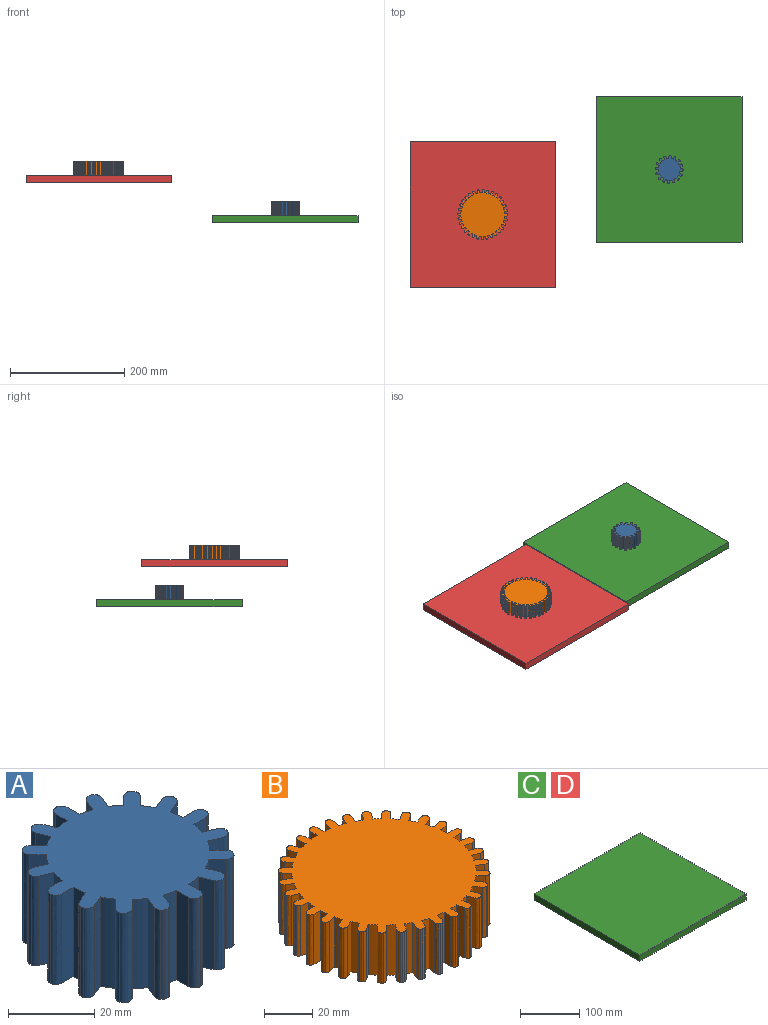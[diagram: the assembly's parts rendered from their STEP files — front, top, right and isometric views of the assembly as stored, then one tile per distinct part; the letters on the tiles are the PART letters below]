
ASSEMBLY  parts=4 mates=2
PART A: 114 faces, bbox 49.3x49.3x25.4 mm
  f0: plane 25.4x3.81mm, normal (-1,0,0), area 96.8mm2, adj f5,f6,f7,f8
  f1: plane 25.4x4.01mm, normal (1,0,0), area 101.9mm2, adj f2,f6,f7,f9
  f2: extruded ~25.4x1.56mm, area 48.5mm2, adj f1,f3,f6,f7
  f3: extruded ~25.4x0.92mm, area 24.5mm2, adj f2,f4,f6,f7
  f4: extruded ~25.4x0.92mm, area 24.5mm2, adj f3,f5,f6,f7
  f5: extruded ~25.4x1.57mm, area 48.5mm2, adj f0,f4,f6,f7
  f6: plane 49.31x49.31mm, normal (0,0,1), area 1458.4mm2, adj f0,f1,f2,f3,f4,f5,f8,f9
  f7: plane 49.31x49.31mm, normal (0,0,-1), area 1458.4mm2, adj f0,f1,f2,f3,f4,f5,f8,f9
  f8: cylinder r=19.05mm len=25.4mm, axis (0,0,-1), area 93mm2, adj f0,f6,f7,f109
  f9: cylinder r=19.05mm len=25.4mm, axis (0,0,-1), area 93mm2, adj f1,f6,f7,f24
  f10: cylinder r=19.05mm len=25.4mm, axis (0,0,-1), area 93mm2, adj f6,f7,f103,f108
  f11: cylinder r=19.05mm len=25.4mm, axis (0,0,-1), area 93mm2, adj f6,f7,f97,f102
  f12: cylinder r=19.05mm len=25.4mm, axis (0,0,-1), area 93mm2, adj f6,f7,f91,f96
  f13: cylinder r=19.05mm len=25.4mm, axis (0,0,-1), area 93mm2, adj f6,f7,f85,f90
  f14: cylinder r=19.05mm len=25.4mm, axis (0,0,-1), area 93mm2, adj f6,f7,f79,f84
  f15: cylinder r=19.05mm len=25.4mm, axis (0,0,-1), area 93mm2, adj f6,f7,f73,f78
  f16: cylinder r=19.05mm len=25.4mm, axis (0,0,-1), area 93mm2, adj f6,f7,f67,f72
  f17: cylinder r=19.05mm len=25.4mm, axis (0,0,-1), area 93mm2, adj f6,f7,f61,f66
  f18: cylinder r=19.05mm len=25.4mm, axis (0,0,-1), area 93mm2, adj f6,f7,f55,f60
  f19: cylinder r=19.05mm len=25.4mm, axis (0,0,-1), area 93mm2, adj f6,f7,f49,f54
  f20: cylinder r=19.05mm len=25.4mm, axis (0,0,-1), area 93mm2, adj f6,f7,f43,f48
  f21: cylinder r=19.05mm len=25.4mm, axis (0,0,-1), area 93mm2, adj f6,f7,f37,f42
  f22: cylinder r=19.05mm len=25.4mm, axis (0,0,-1), area 93mm2, adj f6,f7,f31,f36
  f23: cylinder r=19.05mm len=25.4mm, axis (0,0,-1), area 93mm2, adj f6,f7,f25,f30
  f24: plane 25.4x3.52mm, normal (-0.92,0.38,0), area 96.8mm2, adj f6,f7,f9,f29
  f25: plane 25.4x3.71mm, normal (0.92,-0.38,0), area 101.9mm2, adj f6,f7,f23,f26
  f26: extruded ~25.4x1.82mm, area 48.5mm2, adj f6,f7,f25,f27
  f27: extruded ~25.4x0.76mm, area 24.5mm2, adj f6,f7,f26,f28
  f28: extruded ~25.4x0.94mm, area 24.5mm2, adj f6,f7,f27,f29
  f29: extruded ~25.4x1.51mm, area 48.5mm2, adj f6,f7,f24,f28
  f30: plane 25.4x2.69mm, normal (-0.71,0.71,0), area 96.8mm2, adj f6,f7,f23,f35
  f31: plane 25.4x2.84mm, normal (0.71,-0.71,0), area 101.9mm2, adj f6,f7,f22,f32
  f32: extruded ~25.4x1.8mm, area 48.5mm2, adj f6,f7,f31,f33
  f33: extruded ~25.4x0.82mm, area 24.5mm2, adj f6,f7,f32,f34
  f34: extruded ~25.4x0.82mm, area 24.5mm2, adj f6,f7,f33,f35
  f35: extruded ~25.4x1.8mm, area 48.5mm2, adj f6,f7,f30,f34
  f36: plane 25.4x3.52mm, normal (-0.38,0.92,0), area 96.8mm2, adj f6,f7,f22,f41
  f37: plane 25.4x3.71mm, normal (0.38,-0.92,0), area 101.9mm2, adj f6,f7,f21,f38
  f38: extruded ~25.4x1.51mm, area 48.5mm2, adj f6,f7,f37,f39
  f39: extruded ~25.4x0.94mm, area 24.5mm2, adj f6,f7,f38,f40
  f40: extruded ~25.4x0.76mm, area 24.5mm2, adj f6,f7,f39,f41
  f41: extruded ~25.4x1.82mm, area 48.5mm2, adj f6,f7,f36,f40
  f42: plane 25.4x3.81mm, normal (0,1,0), area 96.8mm2, adj f6,f7,f21,f47
  f43: plane 25.4x4.01mm, normal (0,-1,0), area 101.9mm2, adj f6,f7,f20,f44
  f44: extruded ~25.4x1.56mm, area 48.5mm2, adj f6,f7,f43,f45
  f45: extruded ~25.4x0.92mm, area 24.5mm2, adj f6,f7,f44,f46
  f46: extruded ~25.4x0.92mm, area 24.5mm2, adj f6,f7,f45,f47
  f47: extruded ~25.4x1.57mm, area 48.5mm2, adj f6,f7,f42,f46
  f48: plane 25.4x3.52mm, normal (0.38,0.92,0), area 96.8mm2, adj f6,f7,f20,f53
  f49: plane 25.4x3.71mm, normal (-0.38,-0.92,0), area 101.9mm2, adj f6,f7,f19,f50
  f50: extruded ~25.4x1.82mm, area 48.5mm2, adj f6,f7,f49,f51
  f51: extruded ~25.4x0.76mm, area 24.5mm2, adj f6,f7,f50,f52
  f52: extruded ~25.4x0.94mm, area 24.5mm2, adj f6,f7,f51,f53
  f53: extruded ~25.4x1.51mm, area 48.5mm2, adj f6,f7,f48,f52
  f54: plane 25.4x2.69mm, normal (0.71,0.71,0), area 96.8mm2, adj f6,f7,f19,f59
  f55: plane 25.4x2.84mm, normal (-0.71,-0.71,0), area 101.9mm2, adj f6,f7,f18,f56
  f56: extruded ~25.4x1.8mm, area 48.5mm2, adj f6,f7,f55,f57
  f57: extruded ~25.4x0.82mm, area 24.5mm2, adj f6,f7,f56,f58
  f58: extruded ~25.4x0.82mm, area 24.5mm2, adj f6,f7,f57,f59
  f59: extruded ~25.4x1.8mm, area 48.5mm2, adj f6,f7,f54,f58
  f60: plane 25.4x3.52mm, normal (0.92,0.38,0), area 96.8mm2, adj f6,f7,f18,f65
  f61: plane 25.4x3.71mm, normal (-0.92,-0.38,0), area 101.9mm2, adj f6,f7,f17,f62
  f62: extruded ~25.4x1.51mm, area 48.5mm2, adj f6,f7,f61,f63
  f63: extruded ~25.4x0.94mm, area 24.5mm2, adj f6,f7,f62,f64
  f64: extruded ~25.4x0.76mm, area 24.5mm2, adj f6,f7,f63,f65
  f65: extruded ~25.4x1.82mm, area 48.5mm2, adj f6,f7,f60,f64
  f66: plane 25.4x3.81mm, normal (1,0,0), area 96.8mm2, adj f6,f7,f17,f71
  f67: plane 25.4x4.01mm, normal (-1,0,0), area 101.9mm2, adj f6,f7,f16,f68
  f68: extruded ~25.4x1.56mm, area 48.5mm2, adj f6,f7,f67,f69
  f69: extruded ~25.4x0.92mm, area 24.5mm2, adj f6,f7,f68,f70
  f70: extruded ~25.4x0.92mm, area 24.5mm2, adj f6,f7,f69,f71
  f71: extruded ~25.4x1.57mm, area 48.5mm2, adj f6,f7,f66,f70
  f72: plane 25.4x3.52mm, normal (0.92,-0.38,0), area 96.8mm2, adj f6,f7,f16,f77
  f73: plane 25.4x3.71mm, normal (-0.92,0.38,0), area 101.9mm2, adj f6,f7,f15,f74
  f74: extruded ~25.4x1.82mm, area 48.5mm2, adj f6,f7,f73,f75
  f75: extruded ~25.4x0.76mm, area 24.5mm2, adj f6,f7,f74,f76
  f76: extruded ~25.4x0.94mm, area 24.5mm2, adj f6,f7,f75,f77
  f77: extruded ~25.4x1.51mm, area 48.5mm2, adj f6,f7,f72,f76
  f78: plane 25.4x2.69mm, normal (0.71,-0.71,0), area 96.8mm2, adj f6,f7,f15,f83
  f79: plane 25.4x2.84mm, normal (-0.71,0.71,0), area 101.9mm2, adj f6,f7,f14,f80
  f80: extruded ~25.4x1.8mm, area 48.5mm2, adj f6,f7,f79,f81
  f81: extruded ~25.4x0.82mm, area 24.5mm2, adj f6,f7,f80,f82
  f82: extruded ~25.4x0.82mm, area 24.5mm2, adj f6,f7,f81,f83
  f83: extruded ~25.4x1.8mm, area 48.5mm2, adj f6,f7,f78,f82
  f84: plane 25.4x3.52mm, normal (0.38,-0.92,0), area 96.8mm2, adj f6,f7,f14,f89
  f85: plane 25.4x3.71mm, normal (-0.38,0.92,0), area 101.9mm2, adj f6,f7,f13,f86
  f86: extruded ~25.4x1.51mm, area 48.5mm2, adj f6,f7,f85,f87
  f87: extruded ~25.4x0.94mm, area 24.5mm2, adj f6,f7,f86,f88
  f88: extruded ~25.4x0.76mm, area 24.5mm2, adj f6,f7,f87,f89
  f89: extruded ~25.4x1.82mm, area 48.5mm2, adj f6,f7,f84,f88
  f90: plane 25.4x3.81mm, normal (0,-1,0), area 96.8mm2, adj f6,f7,f13,f95
  f91: plane 25.4x4.01mm, normal (0,1,0), area 101.9mm2, adj f6,f7,f12,f92
  f92: extruded ~25.4x1.56mm, area 48.5mm2, adj f6,f7,f91,f93
  f93: extruded ~25.4x0.92mm, area 24.5mm2, adj f6,f7,f92,f94
  f94: extruded ~25.4x0.92mm, area 24.5mm2, adj f6,f7,f93,f95
  f95: extruded ~25.4x1.57mm, area 48.5mm2, adj f6,f7,f90,f94
  f96: plane 25.4x3.52mm, normal (-0.38,-0.92,0), area 96.8mm2, adj f6,f7,f12,f101
  f97: plane 25.4x3.71mm, normal (0.38,0.92,0), area 101.9mm2, adj f6,f7,f11,f98
  f98: extruded ~25.4x1.82mm, area 48.5mm2, adj f6,f7,f97,f99
  f99: extruded ~25.4x0.76mm, area 24.5mm2, adj f6,f7,f98,f100
  f100: extruded ~25.4x0.94mm, area 24.5mm2, adj f6,f7,f99,f101
  f101: extruded ~25.4x1.51mm, area 48.5mm2, adj f6,f7,f96,f100
  f102: plane 25.4x2.69mm, normal (-0.71,-0.71,0), area 96.8mm2, adj f6,f7,f11,f107
  f103: plane 25.4x2.84mm, normal (0.71,0.71,0), area 101.9mm2, adj f6,f7,f10,f104
  f104: extruded ~25.4x1.8mm, area 48.5mm2, adj f6,f7,f103,f105
  f105: extruded ~25.4x0.82mm, area 24.5mm2, adj f6,f7,f104,f106
  f106: extruded ~25.4x0.82mm, area 24.5mm2, adj f6,f7,f105,f107
  f107: extruded ~25.4x1.8mm, area 48.5mm2, adj f6,f7,f102,f106
  f108: plane 25.4x3.52mm, normal (-0.92,-0.38,0), area 96.8mm2, adj f6,f7,f10,f113
  f109: plane 25.4x3.71mm, normal (0.92,0.38,0), area 101.9mm2, adj f6,f7,f8,f110
  f110: extruded ~25.4x1.51mm, area 48.5mm2, adj f6,f7,f109,f111
  f111: extruded ~25.4x0.94mm, area 24.5mm2, adj f6,f7,f110,f112
  f112: extruded ~25.4x0.76mm, area 24.5mm2, adj f6,f7,f111,f113
  f113: extruded ~25.4x1.82mm, area 48.5mm2, adj f6,f7,f108,f112
PART B: 226 faces, bbox 87.6x87.6x25.4 mm
  f0: plane 25.4x3.91mm, normal (1,0,0), area 99.2mm2, adj f1,f6,f7,f9
  f1: extruded ~25.4x1.66mm, area 50.4mm2, adj f0,f2,f6,f7
  f2: extruded ~25.4x0.95mm, area 25.4mm2, adj f1,f3,f6,f7
  f3: extruded ~25.4x0.95mm, area 25.4mm2, adj f2,f4,f6,f7
  f4: extruded ~25.4x1.66mm, area 50.4mm2, adj f3,f5,f6,f7
  f5: plane 25.4x3.81mm, normal (-1,0,0), area 96.8mm2, adj f4,f6,f7,f8
  f6: plane 87.62x87.62mm, normal (0,0,1), area 5207.3mm2, adj f0,f1,f2,f3,f4,f5,f8,f9
  f7: plane 87.62x87.62mm, normal (0,0,-1), area 5207.3mm2, adj f0,f1,f2,f3,f4,f5,f8,f9
  f8: cylinder r=38.1mm len=25.4mm, axis (0,0,-1), area 93.2mm2, adj f5,f6,f7,f220
  f9: cylinder r=38.1mm len=25.4mm, axis (0,0,-1), area 93.2mm2, adj f0,f6,f7,f45
  f10: cylinder r=38.1mm len=25.4mm, axis (0,0,-1), area 93.2mm2, adj f6,f7,f214,f225
  f11: cylinder r=38.1mm len=25.4mm, axis (0,0,-1), area 93.2mm2, adj f6,f7,f208,f219
  f12: cylinder r=38.1mm len=25.4mm, axis (0,0,-1), area 93.2mm2, adj f6,f7,f202,f213
  f13: cylinder r=38.1mm len=25.4mm, axis (0,0,-1), area 93.2mm2, adj f6,f7,f196,f207
  f14: cylinder r=38.1mm len=25.4mm, axis (0,0,-1), area 93.2mm2, adj f6,f7,f190,f201
  f15: cylinder r=38.1mm len=25.4mm, axis (0,0,-1), area 93.2mm2, adj f6,f7,f184,f195
  f16: cylinder r=38.1mm len=25.4mm, axis (0,0,-1), area 93.2mm2, adj f6,f7,f178,f189
  f17: cylinder r=38.1mm len=25.4mm, axis (0,0,-1), area 93.2mm2, adj f6,f7,f172,f183
  f18: cylinder r=38.1mm len=25.4mm, axis (0,0,-1), area 93.2mm2, adj f6,f7,f166,f177
  f19: cylinder r=38.1mm len=25.4mm, axis (0,0,-1), area 93.2mm2, adj f6,f7,f160,f171
  f20: cylinder r=38.1mm len=25.4mm, axis (0,0,-1), area 93.2mm2, adj f6,f7,f154,f165
  f21: cylinder r=38.1mm len=25.4mm, axis (0,0,-1), area 93.2mm2, adj f6,f7,f148,f159
  f22: cylinder r=38.1mm len=25.4mm, axis (0,0,-1), area 93.2mm2, adj f6,f7,f142,f153
  f23: cylinder r=38.1mm len=25.4mm, axis (0,0,-1), area 93.2mm2, adj f6,f7,f136,f147
  f24: cylinder r=38.1mm len=25.4mm, axis (0,0,-1), area 93.2mm2, adj f6,f7,f130,f141
  f25: cylinder r=38.1mm len=25.4mm, axis (0,0,-1), area 93.2mm2, adj f6,f7,f124,f135
  f26: cylinder r=38.1mm len=25.4mm, axis (0,0,-1), area 93.2mm2, adj f6,f7,f118,f129
  f27: cylinder r=38.1mm len=25.4mm, axis (0,0,-1), area 93.2mm2, adj f6,f7,f112,f123
  f28: cylinder r=38.1mm len=25.4mm, axis (0,0,-1), area 93.2mm2, adj f6,f7,f106,f117
  f29: cylinder r=38.1mm len=25.4mm, axis (0,0,-1), area 93.2mm2, adj f6,f7,f100,f111
  f30: cylinder r=38.1mm len=25.4mm, axis (0,0,-1), area 93.2mm2, adj f6,f7,f94,f105
  f31: cylinder r=38.1mm len=25.4mm, axis (0,0,-1), area 93.2mm2, adj f6,f7,f88,f99
  f32: cylinder r=38.1mm len=25.4mm, axis (0,0,-1), area 93.2mm2, adj f6,f7,f82,f93
  f33: cylinder r=38.1mm len=25.4mm, axis (0,0,-1), area 93.2mm2, adj f6,f7,f76,f87
  f34: cylinder r=38.1mm len=25.4mm, axis (0,0,-1), area 93.2mm2, adj f6,f7,f70,f81
  f35: cylinder r=38.1mm len=25.4mm, axis (0,0,-1), area 93.2mm2, adj f6,f7,f64,f75
  f36: cylinder r=38.1mm len=25.4mm, axis (0,0,-1), area 93.2mm2, adj f6,f7,f58,f69
  f37: cylinder r=38.1mm len=25.4mm, axis (0,0,-1), area 93.2mm2, adj f6,f7,f52,f63
  f38: cylinder r=38.1mm len=25.4mm, axis (0,0,-1), area 93.2mm2, adj f6,f7,f46,f57
  f39: cylinder r=38.1mm len=25.4mm, axis (0,0,-1), area 93.2mm2, adj f6,f7,f40,f51
  f40: plane 25.4x3.83mm, normal (0.98,-0.2,0), area 99.2mm2, adj f6,f7,f39,f41
  f41: extruded ~25.4x1.81mm, area 50.4mm2, adj f6,f7,f40,f42
  f42: extruded ~25.4x0.89mm, area 25.4mm2, adj f6,f7,f41,f43
  f43: extruded ~25.4x0.98mm, area 25.4mm2, adj f6,f7,f42,f44
  f44: extruded ~25.4x1.44mm, area 50.4mm2, adj f6,f7,f43,f45
  f45: plane 25.4x3.74mm, normal (-0.98,0.2,0), area 96.8mm2, adj f6,f7,f9,f44
  f46: plane 25.4x3.61mm, normal (0.92,-0.38,0), area 99.2mm2, adj f6,f7,f38,f47
  f47: extruded ~25.4x1.9mm, area 50.4mm2, adj f6,f7,f46,f48
  f48: extruded ~25.4x0.79mm, area 25.4mm2, adj f6,f7,f47,f49
  f49: extruded ~25.4x0.97mm, area 25.4mm2, adj f6,f7,f48,f50
  f50: extruded ~25.4x1.51mm, area 50.4mm2, adj f6,f7,f49,f51
  f51: plane 25.4x3.52mm, normal (-0.92,0.38,0), area 96.8mm2, adj f6,f7,f39,f50
  f52: plane 25.4x3.25mm, normal (0.83,-0.56,0), area 99.2mm2, adj f6,f7,f37,f53
  f53: extruded ~25.4x1.91mm, area 50.4mm2, adj f6,f7,f52,f54
  f54: extruded ~25.4x0.73mm, area 25.4mm2, adj f6,f7,f53,f55
  f55: extruded ~25.4x0.93mm, area 25.4mm2, adj f6,f7,f54,f56
  f56: extruded ~25.4x1.71mm, area 50.4mm2, adj f6,f7,f55,f57
  f57: plane 25.4x3.17mm, normal (-0.83,0.56,0), area 96.8mm2, adj f6,f7,f38,f56
  f58: plane 25.4x2.76mm, normal (0.71,-0.71,0), area 99.2mm2, adj f6,f7,f36,f59
  f59: extruded ~25.4x1.85mm, area 50.4mm2, adj f6,f7,f58,f60
  f60: extruded ~25.4x0.84mm, area 25.4mm2, adj f6,f7,f59,f61
  f61: extruded ~25.4x0.84mm, area 25.4mm2, adj f6,f7,f60,f62
  f62: extruded ~25.4x1.85mm, area 50.4mm2, adj f6,f7,f61,f63
  f63: plane 25.4x2.69mm, normal (-0.71,0.71,0), area 96.8mm2, adj f6,f7,f37,f62
  f64: plane 25.4x3.25mm, normal (0.56,-0.83,0), area 99.2mm2, adj f6,f7,f35,f65
  f65: extruded ~25.4x1.71mm, area 50.4mm2, adj f6,f7,f64,f66
  f66: extruded ~25.4x0.93mm, area 25.4mm2, adj f6,f7,f65,f67
  f67: extruded ~25.4x0.73mm, area 25.4mm2, adj f6,f7,f66,f68
  f68: extruded ~25.4x1.91mm, area 50.4mm2, adj f6,f7,f67,f69
  f69: plane 25.4x3.17mm, normal (-0.56,0.83,0), area 96.8mm2, adj f6,f7,f36,f68
  f70: plane 25.4x3.61mm, normal (0.38,-0.92,0), area 99.2mm2, adj f6,f7,f34,f71
  f71: extruded ~25.4x1.51mm, area 50.4mm2, adj f6,f7,f70,f72
  f72: extruded ~25.4x0.97mm, area 25.4mm2, adj f6,f7,f71,f73
  f73: extruded ~25.4x0.79mm, area 25.4mm2, adj f6,f7,f72,f74
  f74: extruded ~25.4x1.9mm, area 50.4mm2, adj f6,f7,f73,f75
  f75: plane 25.4x3.52mm, normal (-0.38,0.92,0), area 96.8mm2, adj f6,f7,f35,f74
  f76: plane 25.4x3.83mm, normal (0.2,-0.98,0), area 99.2mm2, adj f6,f7,f33,f77
  f77: extruded ~25.4x1.44mm, area 50.4mm2, adj f6,f7,f76,f78
  f78: extruded ~25.4x0.98mm, area 25.4mm2, adj f6,f7,f77,f79
  f79: extruded ~25.4x0.89mm, area 25.4mm2, adj f6,f7,f78,f80
  f80: extruded ~25.4x1.81mm, area 50.4mm2, adj f6,f7,f79,f81
  f81: plane 25.4x3.74mm, normal (-0.2,0.98,0), area 96.8mm2, adj f6,f7,f34,f80
  f82: plane 25.4x3.91mm, normal (0,-1,0), area 99.2mm2, adj f6,f7,f32,f83
  f83: extruded ~25.4x1.66mm, area 50.4mm2, adj f6,f7,f82,f84
  f84: extruded ~25.4x0.95mm, area 25.4mm2, adj f6,f7,f83,f85
  f85: extruded ~25.4x0.95mm, area 25.4mm2, adj f6,f7,f84,f86
  f86: extruded ~25.4x1.66mm, area 50.4mm2, adj f6,f7,f85,f87
  f87: plane 25.4x3.81mm, normal (0,1,0), area 96.8mm2, adj f6,f7,f33,f86
  f88: plane 25.4x3.83mm, normal (-0.2,-0.98,0), area 99.2mm2, adj f6,f7,f31,f89
  f89: extruded ~25.4x1.81mm, area 50.4mm2, adj f6,f7,f88,f90
  f90: extruded ~25.4x0.89mm, area 25.4mm2, adj f6,f7,f89,f91
  f91: extruded ~25.4x0.98mm, area 25.4mm2, adj f6,f7,f90,f92
  f92: extruded ~25.4x1.44mm, area 50.4mm2, adj f6,f7,f91,f93
  f93: plane 25.4x3.74mm, normal (0.2,0.98,0), area 96.8mm2, adj f6,f7,f32,f92
  f94: plane 25.4x3.61mm, normal (-0.38,-0.92,0), area 99.2mm2, adj f6,f7,f30,f95
  f95: extruded ~25.4x1.9mm, area 50.4mm2, adj f6,f7,f94,f96
  f96: extruded ~25.4x0.79mm, area 25.4mm2, adj f6,f7,f95,f97
  f97: extruded ~25.4x0.97mm, area 25.4mm2, adj f6,f7,f96,f98
  f98: extruded ~25.4x1.51mm, area 50.4mm2, adj f6,f7,f97,f99
  f99: plane 25.4x3.52mm, normal (0.38,0.92,0), area 96.8mm2, adj f6,f7,f31,f98
  f100: plane 25.4x3.25mm, normal (-0.56,-0.83,0), area 99.2mm2, adj f6,f7,f29,f101
  f101: extruded ~25.4x1.91mm, area 50.4mm2, adj f6,f7,f100,f102
  f102: extruded ~25.4x0.73mm, area 25.4mm2, adj f6,f7,f101,f103
  f103: extruded ~25.4x0.93mm, area 25.4mm2, adj f6,f7,f102,f104
  f104: extruded ~25.4x1.71mm, area 50.4mm2, adj f6,f7,f103,f105
  f105: plane 25.4x3.17mm, normal (0.56,0.83,0), area 96.8mm2, adj f6,f7,f30,f104
  f106: plane 25.4x2.76mm, normal (-0.71,-0.71,0), area 99.2mm2, adj f6,f7,f28,f107
  f107: extruded ~25.4x1.85mm, area 50.4mm2, adj f6,f7,f106,f108
  f108: extruded ~25.4x0.84mm, area 25.4mm2, adj f6,f7,f107,f109
  f109: extruded ~25.4x0.84mm, area 25.4mm2, adj f6,f7,f108,f110
  f110: extruded ~25.4x1.85mm, area 50.4mm2, adj f6,f7,f109,f111
  f111: plane 25.4x2.69mm, normal (0.71,0.71,0), area 96.8mm2, adj f6,f7,f29,f110
  f112: plane 25.4x3.25mm, normal (-0.83,-0.56,0), area 99.2mm2, adj f6,f7,f27,f113
  f113: extruded ~25.4x1.71mm, area 50.4mm2, adj f6,f7,f112,f114
  f114: extruded ~25.4x0.93mm, area 25.4mm2, adj f6,f7,f113,f115
  f115: extruded ~25.4x0.73mm, area 25.4mm2, adj f6,f7,f114,f116
  f116: extruded ~25.4x1.91mm, area 50.4mm2, adj f6,f7,f115,f117
  f117: plane 25.4x3.17mm, normal (0.83,0.56,0), area 96.8mm2, adj f6,f7,f28,f116
  f118: plane 25.4x3.61mm, normal (-0.92,-0.38,0), area 99.2mm2, adj f6,f7,f26,f119
  f119: extruded ~25.4x1.51mm, area 50.4mm2, adj f6,f7,f118,f120
  f120: extruded ~25.4x0.97mm, area 25.4mm2, adj f6,f7,f119,f121
  f121: extruded ~25.4x0.79mm, area 25.4mm2, adj f6,f7,f120,f122
  f122: extruded ~25.4x1.9mm, area 50.4mm2, adj f6,f7,f121,f123
  f123: plane 25.4x3.52mm, normal (0.92,0.38,0), area 96.8mm2, adj f6,f7,f27,f122
  f124: plane 25.4x3.83mm, normal (-0.98,-0.2,0), area 99.2mm2, adj f6,f7,f25,f125
  f125: extruded ~25.4x1.44mm, area 50.4mm2, adj f6,f7,f124,f126
  f126: extruded ~25.4x0.98mm, area 25.4mm2, adj f6,f7,f125,f127
  f127: extruded ~25.4x0.89mm, area 25.4mm2, adj f6,f7,f126,f128
  f128: extruded ~25.4x1.81mm, area 50.4mm2, adj f6,f7,f127,f129
  f129: plane 25.4x3.74mm, normal (0.98,0.2,0), area 96.8mm2, adj f6,f7,f26,f128
  f130: plane 25.4x3.91mm, normal (-1,0,0), area 99.2mm2, adj f6,f7,f24,f131
  f131: extruded ~25.4x1.66mm, area 50.4mm2, adj f6,f7,f130,f132
  f132: extruded ~25.4x0.95mm, area 25.4mm2, adj f6,f7,f131,f133
  f133: extruded ~25.4x0.95mm, area 25.4mm2, adj f6,f7,f132,f134
  f134: extruded ~25.4x1.66mm, area 50.4mm2, adj f6,f7,f133,f135
  f135: plane 25.4x3.81mm, normal (1,0,0), area 96.8mm2, adj f6,f7,f25,f134
  f136: plane 25.4x3.83mm, normal (-0.98,0.2,0), area 99.2mm2, adj f6,f7,f23,f137
  f137: extruded ~25.4x1.81mm, area 50.4mm2, adj f6,f7,f136,f138
  f138: extruded ~25.4x0.89mm, area 25.4mm2, adj f6,f7,f137,f139
  f139: extruded ~25.4x0.98mm, area 25.4mm2, adj f6,f7,f138,f140
  f140: extruded ~25.4x1.44mm, area 50.4mm2, adj f6,f7,f139,f141
  f141: plane 25.4x3.74mm, normal (0.98,-0.2,0), area 96.8mm2, adj f6,f7,f24,f140
  f142: plane 25.4x3.61mm, normal (-0.92,0.38,0), area 99.2mm2, adj f6,f7,f22,f143
  f143: extruded ~25.4x1.9mm, area 50.4mm2, adj f6,f7,f142,f144
  f144: extruded ~25.4x0.79mm, area 25.4mm2, adj f6,f7,f143,f145
  f145: extruded ~25.4x0.97mm, area 25.4mm2, adj f6,f7,f144,f146
  f146: extruded ~25.4x1.51mm, area 50.4mm2, adj f6,f7,f145,f147
  f147: plane 25.4x3.52mm, normal (0.92,-0.38,0), area 96.8mm2, adj f6,f7,f23,f146
  f148: plane 25.4x3.25mm, normal (-0.83,0.56,0), area 99.2mm2, adj f6,f7,f21,f149
  f149: extruded ~25.4x1.91mm, area 50.4mm2, adj f6,f7,f148,f150
  f150: extruded ~25.4x0.73mm, area 25.4mm2, adj f6,f7,f149,f151
  f151: extruded ~25.4x0.93mm, area 25.4mm2, adj f6,f7,f150,f152
  f152: extruded ~25.4x1.71mm, area 50.4mm2, adj f6,f7,f151,f153
  f153: plane 25.4x3.17mm, normal (0.83,-0.56,0), area 96.8mm2, adj f6,f7,f22,f152
  f154: plane 25.4x2.76mm, normal (-0.71,0.71,0), area 99.2mm2, adj f6,f7,f20,f155
  f155: extruded ~25.4x1.85mm, area 50.4mm2, adj f6,f7,f154,f156
  f156: extruded ~25.4x0.84mm, area 25.4mm2, adj f6,f7,f155,f157
  f157: extruded ~25.4x0.84mm, area 25.4mm2, adj f6,f7,f156,f158
  f158: extruded ~25.4x1.85mm, area 50.4mm2, adj f6,f7,f157,f159
  f159: plane 25.4x2.69mm, normal (0.71,-0.71,0), area 96.8mm2, adj f6,f7,f21,f158
  f160: plane 25.4x3.25mm, normal (-0.56,0.83,0), area 99.2mm2, adj f6,f7,f19,f161
  f161: extruded ~25.4x1.71mm, area 50.4mm2, adj f6,f7,f160,f162
  f162: extruded ~25.4x0.93mm, area 25.4mm2, adj f6,f7,f161,f163
  f163: extruded ~25.4x0.73mm, area 25.4mm2, adj f6,f7,f162,f164
  f164: extruded ~25.4x1.91mm, area 50.4mm2, adj f6,f7,f163,f165
  f165: plane 25.4x3.17mm, normal (0.56,-0.83,0), area 96.8mm2, adj f6,f7,f20,f164
  f166: plane 25.4x3.61mm, normal (-0.38,0.92,0), area 99.2mm2, adj f6,f7,f18,f167
  f167: extruded ~25.4x1.51mm, area 50.4mm2, adj f6,f7,f166,f168
  f168: extruded ~25.4x0.97mm, area 25.4mm2, adj f6,f7,f167,f169
  f169: extruded ~25.4x0.79mm, area 25.4mm2, adj f6,f7,f168,f170
  f170: extruded ~25.4x1.9mm, area 50.4mm2, adj f6,f7,f169,f171
  f171: plane 25.4x3.52mm, normal (0.38,-0.92,0), area 96.8mm2, adj f6,f7,f19,f170
  f172: plane 25.4x3.83mm, normal (-0.2,0.98,0), area 99.2mm2, adj f6,f7,f17,f173
  f173: extruded ~25.4x1.44mm, area 50.4mm2, adj f6,f7,f172,f174
  f174: extruded ~25.4x0.98mm, area 25.4mm2, adj f6,f7,f173,f175
  f175: extruded ~25.4x0.89mm, area 25.4mm2, adj f6,f7,f174,f176
  f176: extruded ~25.4x1.81mm, area 50.4mm2, adj f6,f7,f175,f177
  f177: plane 25.4x3.74mm, normal (0.2,-0.98,0), area 96.8mm2, adj f6,f7,f18,f176
  f178: plane 25.4x3.91mm, normal (0,1,0), area 99.2mm2, adj f6,f7,f16,f179
  f179: extruded ~25.4x1.66mm, area 50.4mm2, adj f6,f7,f178,f180
  f180: extruded ~25.4x0.95mm, area 25.4mm2, adj f6,f7,f179,f181
  f181: extruded ~25.4x0.95mm, area 25.4mm2, adj f6,f7,f180,f182
  f182: extruded ~25.4x1.66mm, area 50.4mm2, adj f6,f7,f181,f183
  f183: plane 25.4x3.81mm, normal (0,-1,0), area 96.8mm2, adj f6,f7,f17,f182
  f184: plane 25.4x3.83mm, normal (0.2,0.98,0), area 99.2mm2, adj f6,f7,f15,f185
  f185: extruded ~25.4x1.81mm, area 50.4mm2, adj f6,f7,f184,f186
  f186: extruded ~25.4x0.89mm, area 25.4mm2, adj f6,f7,f185,f187
  f187: extruded ~25.4x0.98mm, area 25.4mm2, adj f6,f7,f186,f188
  f188: extruded ~25.4x1.44mm, area 50.4mm2, adj f6,f7,f187,f189
  f189: plane 25.4x3.74mm, normal (-0.2,-0.98,0), area 96.8mm2, adj f6,f7,f16,f188
  f190: plane 25.4x3.61mm, normal (0.38,0.92,0), area 99.2mm2, adj f6,f7,f14,f191
  f191: extruded ~25.4x1.9mm, area 50.4mm2, adj f6,f7,f190,f192
  f192: extruded ~25.4x0.79mm, area 25.4mm2, adj f6,f7,f191,f193
  f193: extruded ~25.4x0.97mm, area 25.4mm2, adj f6,f7,f192,f194
  f194: extruded ~25.4x1.51mm, area 50.4mm2, adj f6,f7,f193,f195
  f195: plane 25.4x3.52mm, normal (-0.38,-0.92,0), area 96.8mm2, adj f6,f7,f15,f194
  f196: plane 25.4x3.25mm, normal (0.56,0.83,0), area 99.2mm2, adj f6,f7,f13,f197
  f197: extruded ~25.4x1.91mm, area 50.4mm2, adj f6,f7,f196,f198
  f198: extruded ~25.4x0.73mm, area 25.4mm2, adj f6,f7,f197,f199
  f199: extruded ~25.4x0.93mm, area 25.4mm2, adj f6,f7,f198,f200
  f200: extruded ~25.4x1.71mm, area 50.4mm2, adj f6,f7,f199,f201
  f201: plane 25.4x3.17mm, normal (-0.56,-0.83,0), area 96.8mm2, adj f6,f7,f14,f200
  f202: plane 25.4x2.76mm, normal (0.71,0.71,0), area 99.2mm2, adj f6,f7,f12,f203
  f203: extruded ~25.4x1.85mm, area 50.4mm2, adj f6,f7,f202,f204
  f204: extruded ~25.4x0.84mm, area 25.4mm2, adj f6,f7,f203,f205
  f205: extruded ~25.4x0.84mm, area 25.4mm2, adj f6,f7,f204,f206
  f206: extruded ~25.4x1.85mm, area 50.4mm2, adj f6,f7,f205,f207
  f207: plane 25.4x2.69mm, normal (-0.71,-0.71,0), area 96.8mm2, adj f6,f7,f13,f206
  f208: plane 25.4x3.25mm, normal (0.83,0.56,0), area 99.2mm2, adj f6,f7,f11,f209
  f209: extruded ~25.4x1.71mm, area 50.4mm2, adj f6,f7,f208,f210
  f210: extruded ~25.4x0.93mm, area 25.4mm2, adj f6,f7,f209,f211
  f211: extruded ~25.4x0.73mm, area 25.4mm2, adj f6,f7,f210,f212
  f212: extruded ~25.4x1.91mm, area 50.4mm2, adj f6,f7,f211,f213
  f213: plane 25.4x3.17mm, normal (-0.83,-0.56,0), area 96.8mm2, adj f6,f7,f12,f212
  f214: plane 25.4x3.61mm, normal (0.92,0.38,0), area 99.2mm2, adj f6,f7,f10,f215
  f215: extruded ~25.4x1.51mm, area 50.4mm2, adj f6,f7,f214,f216
  f216: extruded ~25.4x0.97mm, area 25.4mm2, adj f6,f7,f215,f217
  f217: extruded ~25.4x0.79mm, area 25.4mm2, adj f6,f7,f216,f218
  f218: extruded ~25.4x1.9mm, area 50.4mm2, adj f6,f7,f217,f219
  f219: plane 25.4x3.52mm, normal (-0.92,-0.38,0), area 96.8mm2, adj f6,f7,f11,f218
  f220: plane 25.4x3.83mm, normal (0.98,0.2,0), area 99.2mm2, adj f6,f7,f8,f221
  f221: extruded ~25.4x1.44mm, area 50.4mm2, adj f6,f7,f220,f222
  f222: extruded ~25.4x0.98mm, area 25.4mm2, adj f6,f7,f221,f223
  f223: extruded ~25.4x0.89mm, area 25.4mm2, adj f6,f7,f222,f224
  f224: extruded ~25.4x1.81mm, area 50.4mm2, adj f6,f7,f223,f225
  f225: plane 25.4x3.74mm, normal (-0.98,-0.2,0), area 96.8mm2, adj f6,f7,f10,f224
PART C: 6 faces, bbox 254x254x12.7 mm
  f0: plane 254x12.7mm, normal (-1,0,0), area 3225.8mm2, adj f1,f3,f4,f5
  f1: plane 254x12.7mm, normal (0,-1,0), area 3225.8mm2, adj f0,f2,f4,f5
  f2: plane 254x12.7mm, normal (1,0,0), area 3225.8mm2, adj f1,f3,f4,f5
  f3: plane 254x12.7mm, normal (0,1,0), area 3225.8mm2, adj f0,f2,f4,f5
  f4: plane 254x254mm, normal (0,0,1), area 64516mm2, adj f0,f1,f2,f3
  f5: plane 254x254mm, normal (0,0,-1), area 64516mm2, adj f0,f1,f2,f3
PART D: same geometry as C
PLACE A rot(axis=(0,0,1),44.4deg) t=(269.22,5.92,-60.67)mm
PLACE B rot(axis=(0,0,1),112.8deg) t=(-56.94,-73.1,9.52)mm
PLACE C t=(307.08,-9.62,-73.37)mm
PLACE D t=(-19.08,-88.63,-3.18)mm fixed
MATE revolute B.f8 <-> D.f4  axis (0,0,-1) through (-56.94,-73.1,9.52)mm
MATE revolute A.f8 <-> C.f4  axis (0,0,-1) through (269.22,5.92,-60.67)mm
